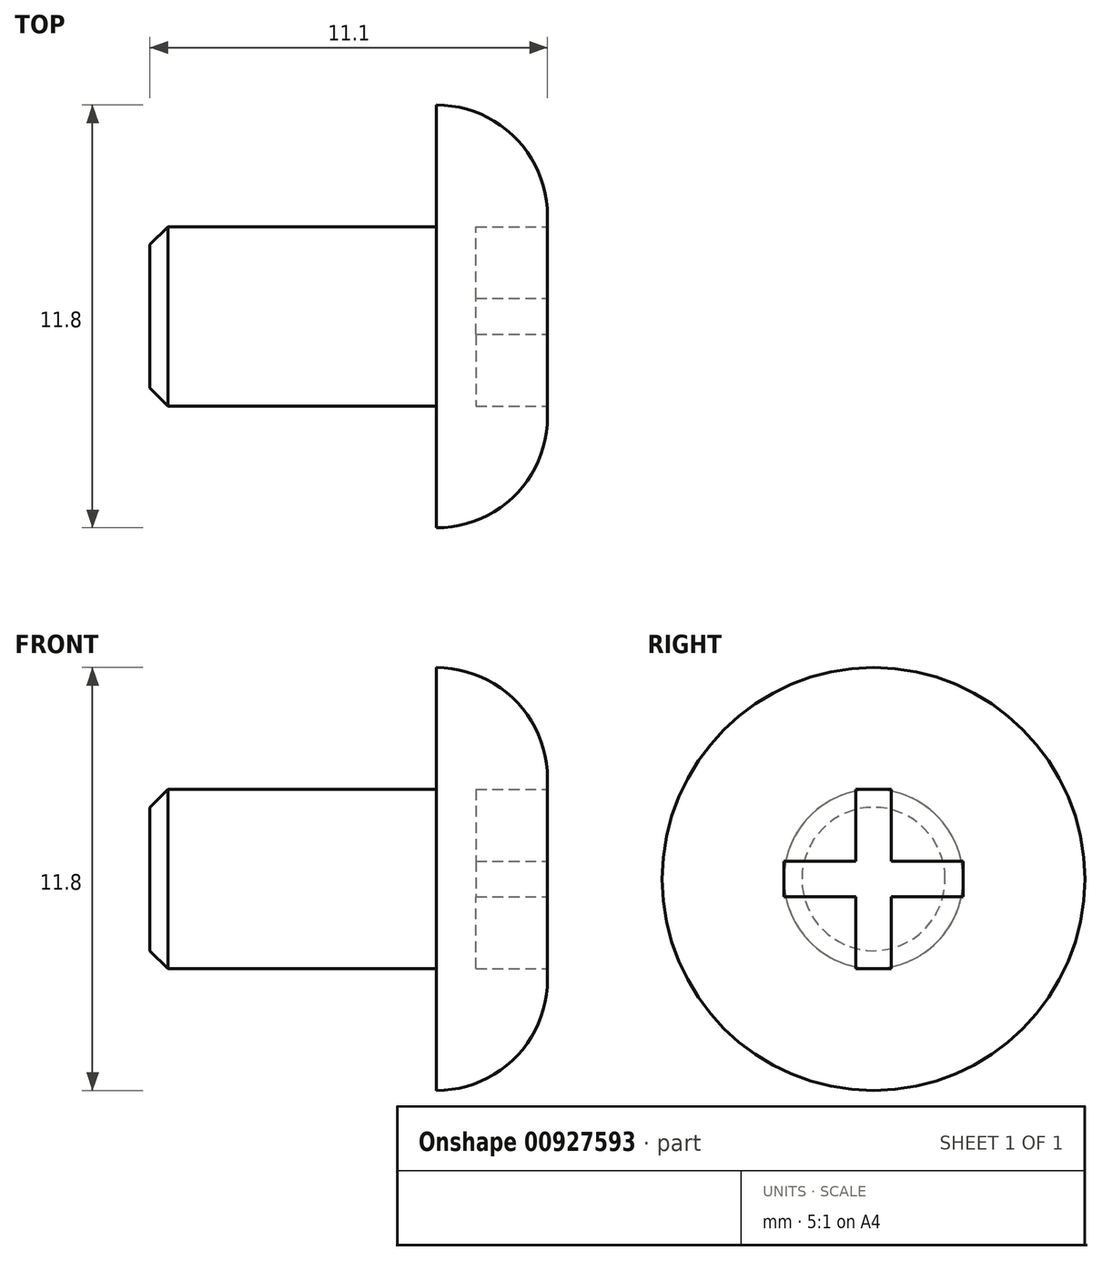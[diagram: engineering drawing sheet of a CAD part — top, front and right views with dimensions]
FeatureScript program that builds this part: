
annotation { "Feature Type Name" : "Feature", "Feature Type Description" : "" }
export const myFeature = defineFeature(function(context is Context, id is Id, definition is map)
    precondition{}
    {
        {
            var Q0;
            Q0=qCreatedBy(makeId("Right.planeOp"),FACE);
            var sketch = newSketch(context, id + "F0", { "sketchPlane" : qUnion([Q0])});
            skCircle(sketch, "E0", {"center": v(0, 0) * mm, "radius": 5.9 * mm});
            skSolve(sketch);
        }
        {
            var Q0;
            Q0 = qSketchRegion(id + "F0", true);
            extrude(context, id + "F1", {"entities" : qUnion([Q0]), "oppositeDirection" : true, "depth" : 3.1 * mm, "offsetDistance" : 25 * mm});
        }
        {
            var Q0;
            Q0=makeQuery(id+"F1.opExtrude","CAP_EDGE",EDGE,{"disambiguationData":[OSD([sQuery(id+"F0.wireOp",EDGE,"E0")])],"isStart":true});
            fillet(context, id + "F2", {"entities" : qUnion([Q0]), "radius" : 3.1 * mm, "tangentPropagation" : true, "allowEdgeOverflow" : false});
        }
        {
            var Q0;
            Q0=makeQuery(id+"F1.opExtrude","CAP_FACE",FACE,{"disambiguationData":[OSD([sQuery(id+"F0.wireOp",EDGE,"E0")])],"isStart":true});
            var sketch = newSketch(context, id + "F3", { "sketchPlane" : qUnion([Q0])});
            skLineSegment(sketch, "E1", {"start": v(-8.6, 0) * mm, "end": v(9.28, 0) * mm, "construction": true});
            skLineSegment(sketch, "E2", {"start": v(0, 8.2) * mm, "end": v(0, -8.66) * mm, "construction": true});
            skLineSegment(sketch, "E3", {"start": v(0, 2.5) * mm, "end": v(0.5, 2.5) * mm});
            skLineSegment(sketch, "E4", {"start": v(0.5, 2.5) * mm, "end": v(0.5, 0.5) * mm});
            skLineSegment(sketch, "E5", {"start": v(0.5, 0.5) * mm, "end": v(2.5, 0.5) * mm});
            skLineSegment(sketch, "E6", {"start": v(2.5, 0.5) * mm, "end": v(2.5, 0) * mm});
            skLineSegment(sketch, "E7.MirrorCS", {"start": v(0, 2.5) * mm, "end": v(-0.5, 2.5) * mm});
            skLineSegment(sketch, "E8.MirrorCS", {"start": v(-0.5, 2.5) * mm, "end": v(-0.5, 0.5) * mm});
            skLineSegment(sketch, "E9.MirrorCS", {"start": v(-0.5, 0.5) * mm, "end": v(-2.5, 0.5) * mm});
            skLineSegment(sketch, "E10.MirrorCS", {"start": v(-2.5, 0.5) * mm, "end": v(-2.5, 0) * mm});
            skLineSegment(sketch, "E11.MirrorCS", {"start": v(-2.5, -0.5) * mm, "end": v(-2.5, 0) * mm});
            skLineSegment(sketch, "E12.MirrorCS", {"start": v(-0.5, -0.5) * mm, "end": v(-2.5, -0.5) * mm});
            skLineSegment(sketch, "E13.MirrorCS", {"start": v(-0.5, -2.5) * mm, "end": v(-0.5, -0.5) * mm});
            skLineSegment(sketch, "E14.MirrorCS", {"start": v(0, -2.5) * mm, "end": v(-0.5, -2.5) * mm});
            skLineSegment(sketch, "E15.MirrorCS", {"start": v(0, -2.5) * mm, "end": v(0.5, -2.5) * mm});
            skLineSegment(sketch, "E16.MirrorCS", {"start": v(0.5, -2.5) * mm, "end": v(0.5, -0.5) * mm});
            skLineSegment(sketch, "E17.MirrorCS", {"start": v(0.5, -0.5) * mm, "end": v(2.5, -0.5) * mm});
            skLineSegment(sketch, "E18.MirrorCS", {"start": v(2.5, -0.5) * mm, "end": v(2.5, 0) * mm});
            skSolve(sketch);
        }
        {
            var Q0;
            Q0 = qSketchRegion(id + "F3", true);
            extrude(context, id + "F4", {"entities" : qUnion([Q0]), "operationType" : NewBodyOperationType.REMOVE, "oppositeDirection" : true, "depth" : 2 * mm, "offsetDistance" : 25 * mm});
        }
        {
            var Q0;
            Q0=makeQuery(id+"F1.opExtrude","CAP_FACE",FACE,{"disambiguationData":[OSD([sQuery(id+"F0.wireOp",EDGE,"E0")])],"isStart":false});
            var sketch = newSketch(context, id + "F5", { "sketchPlane" : qUnion([Q0])});
            skCircle(sketch, "E19", {"center": v(0, 0) * mm, "radius": 2.5 * mm});
            skSolve(sketch);
        }
        {
            var Q0;
            Q0 = qSketchRegion(id + "F5", true);
            extrude(context, id + "F6", {"entities" : qUnion([Q0]), "operationType" : NewBodyOperationType.ADD, "depth" : 8 * mm, "offsetDistance" : 25 * mm});
        }
        {
            var Q0;
            Q0=makeQuery(id+"F6.opExtrude","CAP_EDGE",EDGE,{"disambiguationData":[OSD([sQuery(id+"F5.wireOp",EDGE,"E19")])],"isStart":false});
            chamfer(context, id + "F7", {"entities" : qUnion([Q0]), "width" : 0.5 * mm, "tangentPropagation" : true});
        }
    });
